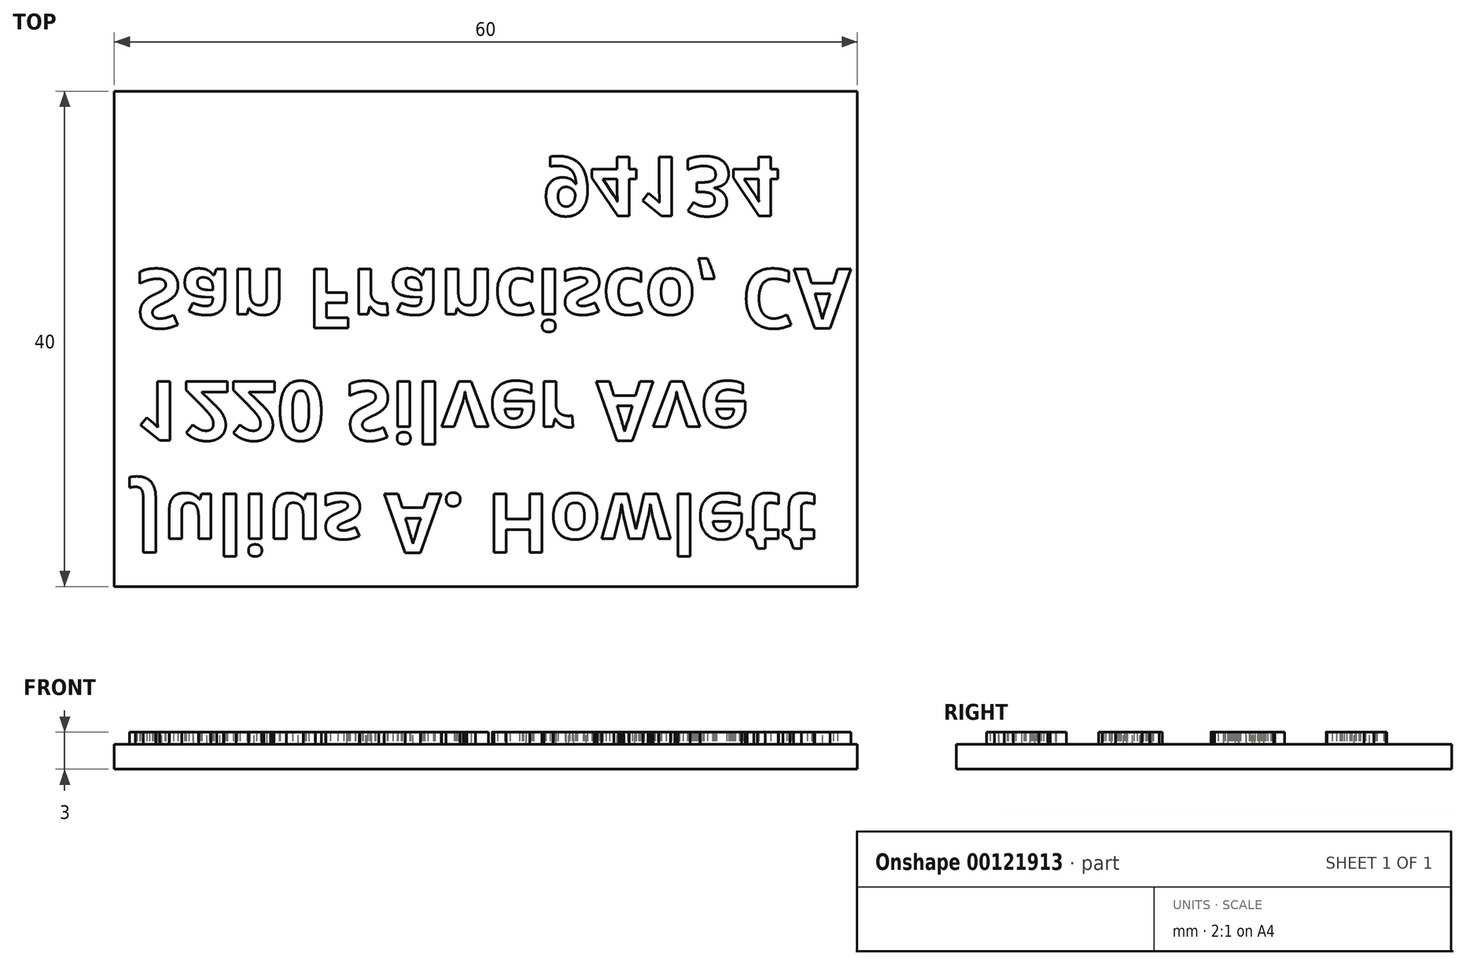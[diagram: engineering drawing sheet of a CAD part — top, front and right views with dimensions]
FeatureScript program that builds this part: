
annotation { "Feature Type Name" : "Feature", "Feature Type Description" : "" }
export const myFeature = defineFeature(function(context is Context, id is Id, definition is map)
    precondition{}
    {
        {
            var Q0;
            Q0=qCreatedBy(makeId("Top.planeOp"),FACE);
            var sketch = newSketch(context, id + "F0", { "sketchPlane" : qUnion([Q0])});
            skLineSegment(sketch, "E0.bottom", {"start": v(30, -20) * mm, "end": v(-30, -20) * mm});
            skLineSegment(sketch, "E0.top", {"start": v(30, 20) * mm, "end": v(-30, 20) * mm});
            skLineSegment(sketch, "E0.left", {"start": v(30, -20) * mm, "end": v(30, 20) * mm});
            skLineSegment(sketch, "E0.right", {"start": v(-30, -20) * mm, "end": v(-30, 20) * mm});
            skPoint(sketch, "E0.middle", {"position": v(0, 0) * mm});
            skSolve(sketch);
        }
        {
            var Q0;
            Q0 = qSketchRegion(id + "F0", true);
            extrude(context, id + "F1", {"entities" : qUnion([Q0]), "depth" : 2 * mm});
        }
        {
            var Q0;
            Q0=makeQuery(id+"F1.opExtrude","CAP_FACE",FACE,{"disambiguationData":[OSD([sQuery(id+"F0.wireOp",EDGE,"E0.bottom"),sQuery(id+"F0.wireOp",EDGE,"E0.top"),sQuery(id+"F0.wireOp",EDGE,"E0.left"),sQuery(id+"F0.wireOp",EDGE,"E0.right")])],"isStart":true});
            cPlane(context, id + "F2", {"entities" : qUnion([Q0]), "cplaneType" : CPlaneType.OFFSET, "offset" : 2 * mm, "oppositeDirection" : true, "width" : 150 * mm, "height" : 150 * mm});
        }
        {
            var Q0;
            Q0=qCreatedBy(id+"F2.planeOp",FACE);
            var sketch = newSketch(context, id + "F3", { "sketchPlane" : qUnion([Q0])});
            skText(sketch, "E1", { "text": " Julius A. Howlett\n 1220 Silver Ave\n San Francisco, CA\n                    94134", "fontName": "OpenSans-Bold.ttf"});
            skPoint(sketch, "E2.0", {"position": v(-30, 20) * mm});
            skPoint(sketch, "E3.0", {"position": v(30, -20) * mm});
            const initialGuessF3  = {"E1": [-0.03, 0.0125, 1, 0, 0.0048]};
            skSetInitialGuess(sketch, initialGuessF3);
            skSolve(sketch);
        }
        {
            var Q0;
            Q0 = qSketchRegion(id + "F3", true);
            extrude(context, id + "F4", {"entities" : qUnion([Q0]), "operationType" : NewBodyOperationType.ADD, "oppositeDirection" : true, "depth" : 1 * mm});
        }
    });
